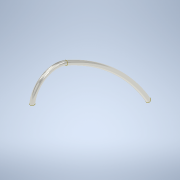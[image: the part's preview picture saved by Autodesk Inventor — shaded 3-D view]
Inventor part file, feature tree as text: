
AUTODESK INVENTOR PART (.ipt)
format: ipt  version: 2022 (Build 260153000, 153)  size: 137,216 bytes
history: native  units: in
note: dims shown in document units (in); Inventor stores cm internally (conversion verified against a paired STEP export)
features: sketch x2, sweep x1
ambient origin geometry x8: Origin, YZ Plane, XZ Plane, XY Plane, X Axis, Y Axis, Z Axis, Center Point
bodies: Solid1 (feature_tree)
feature tree (3):
  sweep  "Sweep1"
  sketch  "Sketch3"  dims[d10=0.001in d11=0.0059in]
  sketch  "Sketch4"  dims[d12=0.013in d13=0.0217in d14=90.0deg d15=0.0in d16=0.0in]
